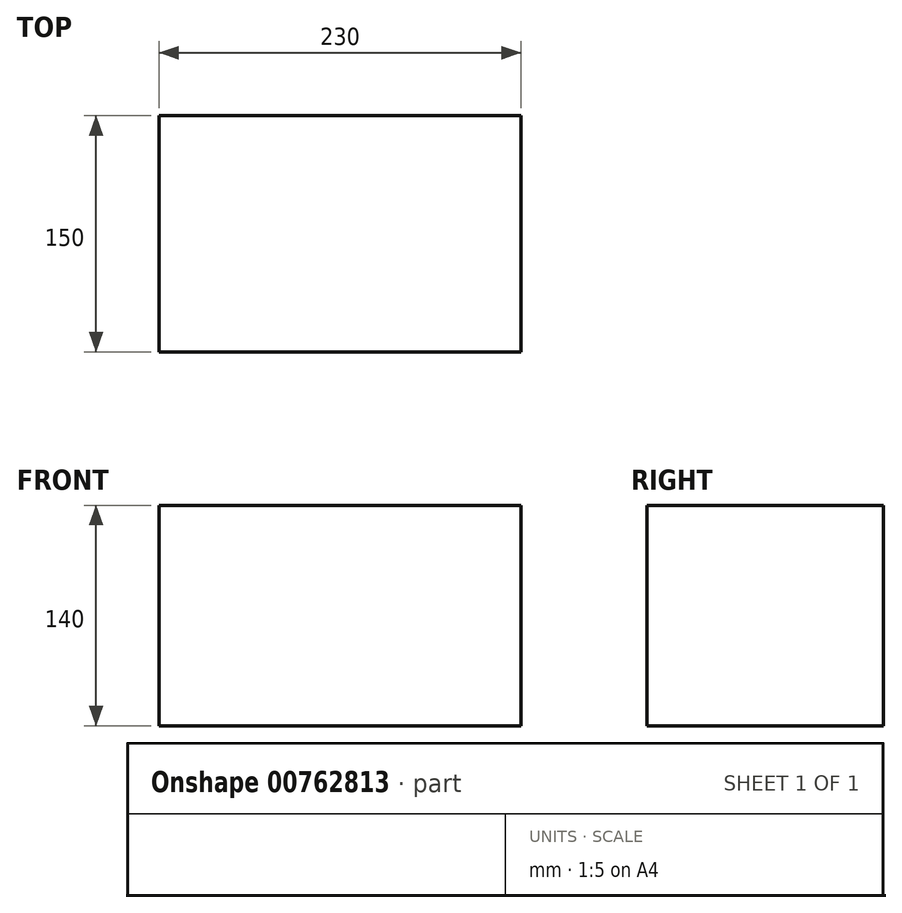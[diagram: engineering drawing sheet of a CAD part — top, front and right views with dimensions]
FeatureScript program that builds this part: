
annotation { "Feature Type Name" : "Feature", "Feature Type Description" : "" }
export const myFeature = defineFeature(function(context is Context, id is Id, definition is map)
    precondition{}
    {
        {
            var Q0;
            Q0=qCreatedBy(makeId("Top.planeOp"),FACE);
            var sketch = newSketch(context, id + "F0", { "sketchPlane" : qUnion([Q0])});
            skLineSegment(sketch, "E0.bottom", {"start": v(-115, 75) * mm, "end": v(115, 75) * mm});
            skLineSegment(sketch, "E0.top", {"start": v(-115, -75) * mm, "end": v(115, -75) * mm});
            skLineSegment(sketch, "E0.left", {"start": v(-115, 75) * mm, "end": v(-115, -75) * mm});
            skLineSegment(sketch, "E0.right", {"start": v(115, 75) * mm, "end": v(115, -75) * mm});
            skPoint(sketch, "E0.middle", {"position": v(0, 0) * mm});
            skSolve(sketch);
        }
        {
            var Q0;
            Q0=makeQuery(id+"F0.imprint","IMPRINT",FACE,{"disambiguationData":[TD([[makeQuery(id+"F0.imprint","IMPRINT",EDGE,{"derivedFrom":sQuery(id+"F0.wireOp",EDGE,"E0.bottom")}),-1.0]])]});
            extrude(context, id + "F1", {"entities" : qUnion([Q0]), "depth" : 140 * mm, "offsetDistance" : 25.4 * mm});
        }
    });
